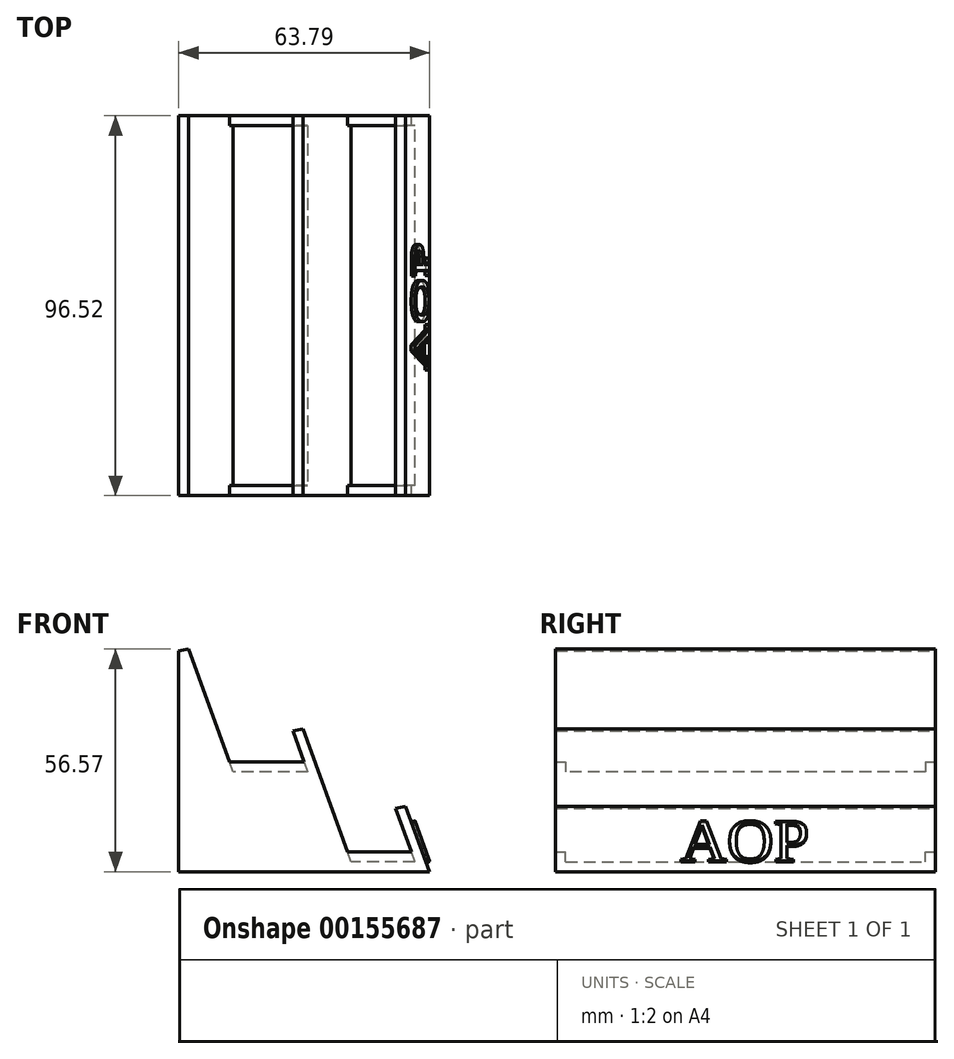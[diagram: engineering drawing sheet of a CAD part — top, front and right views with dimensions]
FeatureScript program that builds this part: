
annotation { "Feature Type Name" : "Feature", "Feature Type Description" : "" }
export const myFeature = defineFeature(function(context is Context, id is Id, definition is map)
    precondition{}
    {
        {
            var Q0;
            Q0=qCreatedBy(makeId("Front.planeOp"),FACE);
            var sketch = newSketch(context, id + "F0", { "sketchPlane" : qUnion([Q0])});
            skLineSegment(sketch, "E0", {"start": v(34.66, 0) * mm, "end": v(-29.02, 0) * mm});
            skLineSegment(sketch, "E1", {"start": v(34.66, 0) * mm, "end": v(28.63, 16.55) * mm});
            skLineSegment(sketch, "E2", {"start": v(11.18, 5.08) * mm, "end": v(4.71, 22.86) * mm});
            skLineSegment(sketch, "E3", {"start": v(4.71, 22.86) * mm, "end": v(-16.91, 22.86) * mm});
            skLineSegment(sketch, "E4", {"start": v(-16.91, 22.86) * mm, "end": v(-26.48, 49.14) * mm});
            skLineSegment(sketch, "E5", {"start": v(-29.02, 56.12) * mm, "end": v(-29.02, 0) * mm});
            skLineSegment(sketch, "E6", {"start": v(-26.48, 5.08) * mm, "end": v(11.18, 5.08) * mm});
            skLineSegment(sketch, "E7", {"start": v(-26.48, 5.08) * mm, "end": v(-26.48, 49.14) * mm});
            skLineSegment(sketch, "E8", {"start": v(-26.48, 56.57) * mm, "end": v(-16.06, 27.94) * mm});
            skLineSegment(sketch, "E9", {"start": v(-16.06, 27.94) * mm, "end": v(2.86, 27.94) * mm});
            skLineSegment(sketch, "E10", {"start": v(2.54, 36.25) * mm, "end": v(13.89, 5.08) * mm});
            skLineSegment(sketch, "E11", {"start": v(0, 35.8) * mm, "end": v(2.54, 36.25) * mm});
            skLineSegment(sketch, "E12", {"start": v(-29.02, 56.12) * mm, "end": v(-26.48, 56.57) * mm});
            skLineSegment(sketch, "E13", {"start": v(26.1, 16.1) * mm, "end": v(30.1, 5.08) * mm});
            skLineSegment(sketch, "E14", {"start": v(26.1, 16.1) * mm, "end": v(28.63, 16.55) * mm});
            skPoint(sketch, "E15.orphan", {"position": v(13.03, 0) * mm});
            skPoint(sketch, "E16.orphan", {"position": v(15.73, 0) * mm});
            skLineSegment(sketch, "E17.trimOffspring", {"start": v(13.89, 5.08) * mm, "end": v(30.1, 5.08) * mm});
            skLineSegment(sketch, "E18.trimOffspring", {"start": v(2.86, 27.94) * mm, "end": v(0, 35.8) * mm});
            skPoint(sketch, "E19.orphan", {"position": v(31.95, 0) * mm});
            skPoint(sketch, "E20.orphan", {"position": v(32.8, 5.08) * mm});
            skSolve(sketch);
        }
        {
            var Q0;
            Q0 = qSketchRegion(id + "F0", true);
            extrude(context, id + "F1", {"entities" : qUnion([Q0]), "depth" : 96.52 * mm});
        }
        {
            var Q0;
            Q0=makeQuery(id+"F1.opExtrude","SWEPT_FACE",FACE,{"disambiguationData":[OSD([sQuery(id+"F0.wireOp",EDGE,"E9")])]});
            var Q1;
            Q1=makeQuery(id+"F1.opExtrude","SWEPT_FACE",FACE,{"disambiguationData":[OSD([sQuery(id+"F0.wireOp",EDGE,"E17.trimOffspring")])]});
            shell(context, id + "F2", {"entities" : qUnion([Q0, Q1]), "thickness" : 2.54 * mm});
        }
        {
            var Q0;
            Q0=makeQuery(id+"F1.opExtrude","SWEPT_FACE",FACE,{"disambiguationData":[OSD([sQuery(id+"F0.wireOp",EDGE,"E1")])]});
            var sketch = newSketch(context, id + "F3", { "sketchPlane" : qUnion([Q0])});
            skText(sketch, "E21", { "text": "AOP", "fontName": "Tinos-Regular.ttf"});
            const initialGuessF3  = {"E21": [-0.0648, -0.00924, 1, 0, 0.01177]};
            skSetInitialGuess(sketch, initialGuessF3);
            skSolve(sketch);
        }
        {
            var Q0;
            Q0 = qSketchRegion(id + "F3", true);
            extrude(context, id + "F4", {"entities" : qUnion([Q0]), "operationType" : NewBodyOperationType.ADD, "depth" : 1.02 * mm});
        }
        {
            var Q0;
            Q0=makeQuery(id+"F0.imprint","IMPRINT",FACE,{"disambiguationData":[TD([[makeQuery(id+"F0.imprint","IMPRINT",EDGE,{"derivedFrom":sQuery(id+"F0.wireOp",EDGE,"E2")}),1.0]])]});
            extrude(context, id + "F5", {"entities" : qUnion([Q0]), "operationType" : NewBodyOperationType.ADD, "depth" : 96.52 * mm});
        }
    });
